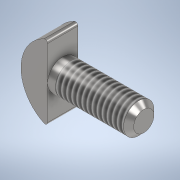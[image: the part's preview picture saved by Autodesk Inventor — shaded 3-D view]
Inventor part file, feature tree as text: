
AUTODESK INVENTOR PART (.ipt)
format: ipt  version: 2021 (Build 250183000, 183)  size: 143,360 bytes
history: native  units: in
note: dims shown in document units (in); Inventor stores cm internally (conversion verified against a paired STEP export)
features: other x2, thread x1
ambient origin geometry x8: Origin, YZ Plane, XZ Plane, XY Plane, X Axis, Y Axis, Z Axis, Center Point
bodies: Body1 (feature_tree)
feature tree (3):
  other  "Sólido2"
  thread  "Rosca1"  [1 undecoded]
  other  "Sólido1"
note: 1 required parameter value undecoded (feature->parameter linkage not recoverable at this tier; creation-order binding heuristic only, values carry confidence <= 0.55)
